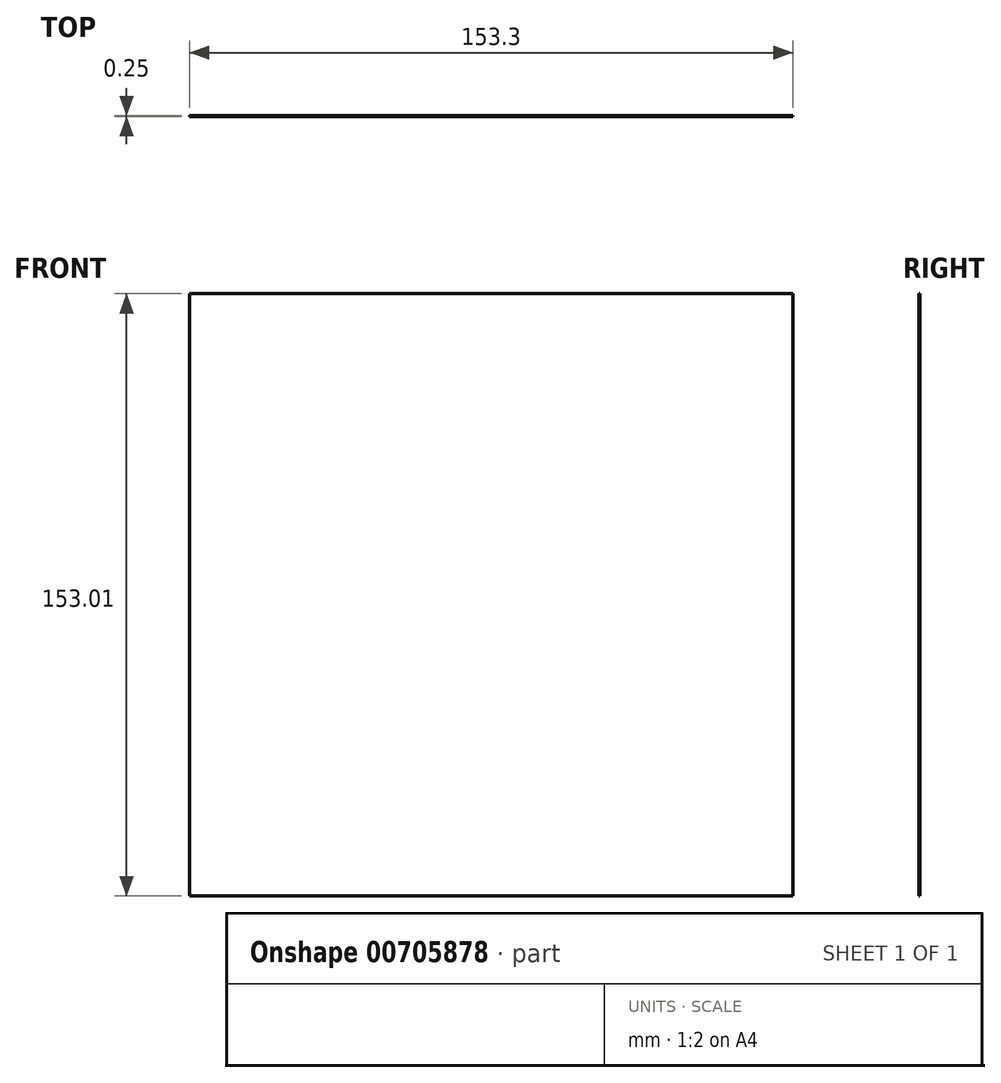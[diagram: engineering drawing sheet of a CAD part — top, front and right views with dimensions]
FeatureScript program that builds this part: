
annotation { "Feature Type Name" : "Feature", "Feature Type Description" : "" }
export const myFeature = defineFeature(function(context is Context, id is Id, definition is map)
    precondition{}
    {
        {
            var Q0;
            Q0=qCreatedBy(makeId("Front.planeOp"),FACE);
            var sketch = newSketch(context, id + "F0", { "sketchPlane" : qUnion([Q0])});
            skLineSegment(sketch, "E0.bottom", {"start": v(-76.65, 76.94) * mm, "end": v(76.65, 76.94) * mm});
            skLineSegment(sketch, "E0.top", {"start": v(-76.65, -76.07) * mm, "end": v(76.65, -76.07) * mm});
            skLineSegment(sketch, "E0.left", {"start": v(-76.65, 76.94) * mm, "end": v(-76.65, -76.07) * mm});
            skLineSegment(sketch, "E0.right", {"start": v(76.65, 76.94) * mm, "end": v(76.65, -76.07) * mm});
            skSolve(sketch);
        }
        {
            var Q0;
            Q0=makeQuery(id+"F0.imprint","IMPRINT",FACE,{"disambiguationData":[TD([[makeQuery(id+"F0.imprint","IMPRINT",EDGE,{"derivedFrom":sQuery(id+"F0.wireOp",EDGE,"E0.bottom")}),-1.0]])]});
            extrude(context, id + "F1", {"entities" : qUnion([Q0]), "depth" : 0.25 * mm, "offsetDistance" : 25.4 * mm});
        }
    });
